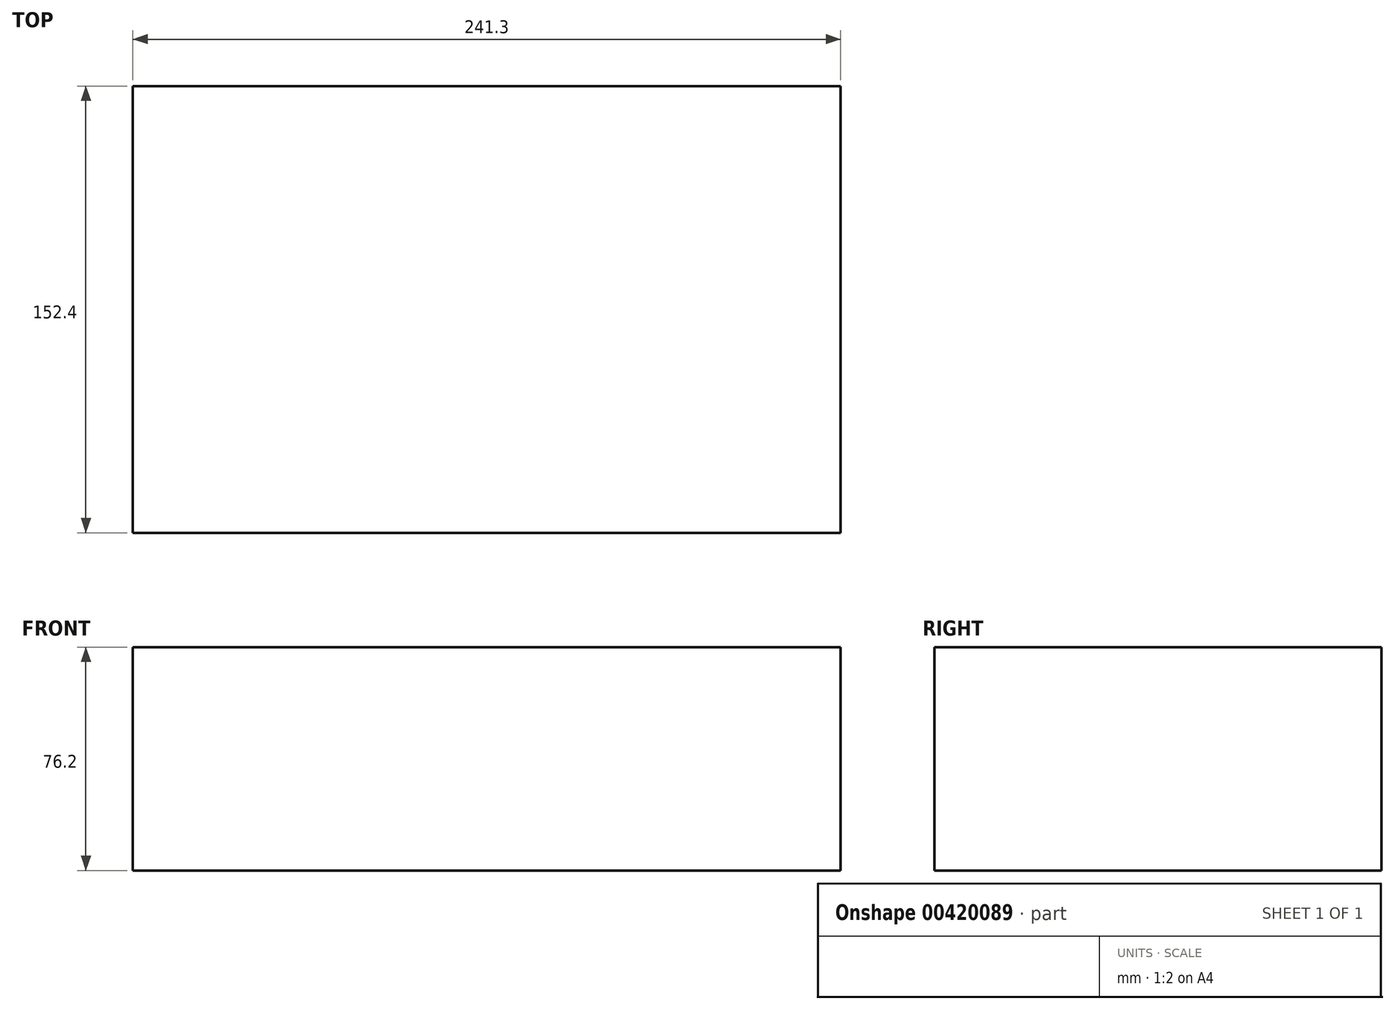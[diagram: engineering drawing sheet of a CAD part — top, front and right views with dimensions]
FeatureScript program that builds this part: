
annotation { "Feature Type Name" : "Feature", "Feature Type Description" : "" }
export const myFeature = defineFeature(function(context is Context, id is Id, definition is map)
    precondition{}
    {
        {
            var Q0;
            Q0=qCreatedBy(makeId("Front.planeOp"),FACE);
            var sketch = newSketch(context, id + "F0", { "sketchPlane" : qUnion([Q0])});
            skLineSegment(sketch, "E0.bottom", {"start": v(-118.87, 44.14) * mm, "end": v(122.43, 44.14) * mm});
            skLineSegment(sketch, "E0.top", {"start": v(-118.87, -32.06) * mm, "end": v(122.43, -32.06) * mm});
            skLineSegment(sketch, "E0.left", {"start": v(-118.87, 44.14) * mm, "end": v(-118.87, -32.06) * mm});
            skLineSegment(sketch, "E0.right", {"start": v(122.43, 44.14) * mm, "end": v(122.43, -32.06) * mm});
            skSolve(sketch);
        }
        {
            var Q0;
            Q0=makeQuery(id+"F0.imprint","IMPRINT",FACE,{"disambiguationData":[TD([[makeQuery(id+"F0.imprint","IMPRINT",EDGE,{"derivedFrom":sQuery(id+"F0.wireOp",EDGE,"E0.bottom")}),-1.0]])]});
            extrude(context, id + "F1", {"entities" : qUnion([Q0]), "depth" : 152.4 * mm});
        }
    });
